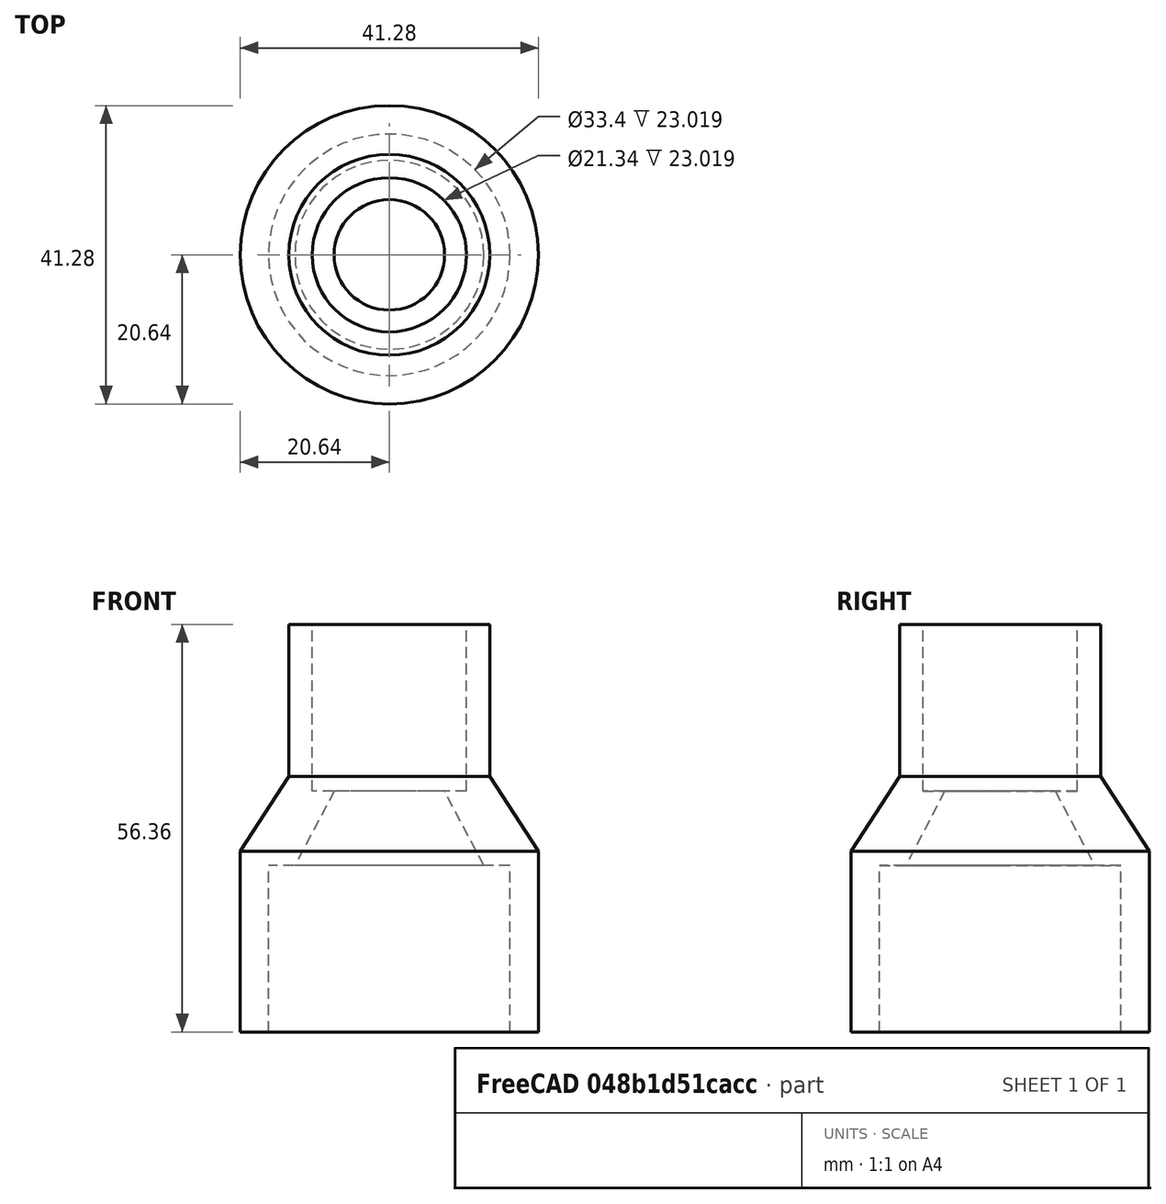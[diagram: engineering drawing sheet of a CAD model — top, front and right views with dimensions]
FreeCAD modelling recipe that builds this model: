
FCSTD DOCUMENT  (FreeCAD 0.17R13303 (Git))
Label: coupling-test
License: All rights reserved
LicenseURL: http://en.wikipedia.org/wiki/All_rights_reserved
objects: Part::Cylinder×4, Part::Cone×2, Part::MultiFuse×2, Part::Cut×1
note: 9 computed .brp shape members not serialized (recipe doc carries the construction recipe); baked Part::Feature solids carry a one-line shape summary decoded from their .brp

FEATURE [Part::Cylinder] Cylinder1
  Angle = 360
  AttacherType = Attacher::AttachEngine3D
  Height = 25.0057
  Radius = 20.6375
FEATURE [Part::Cone] Cone
  Angle = 360
  AttacherType = Attacher::AttachEngine3D
  Height = 10.3187
  Placement = pos=(0,0,25.0057) rot=(0,0,1;0rad)
  Radius1 = 20.6375
  Radius2 = 13.8906
FEATURE [Part::Cylinder] Cylinder2
  Angle = 360
  AttacherType = Attacher::AttachEngine3D
  Height = 21.0318
  Placement = pos=(0,0,35.3245) rot=(0,0,1;0rad)
  Radius = 13.8906
FEATURE [Part::MultiFuse] OuterParts
  Shapes = -> [Cylinder1,Cone,Cylinder2]
FEATURE [Part::Cylinder] Cylinder1i
  Angle = 360
  AttacherType = Attacher::AttachEngine3D
  Height = 23.0188
  Radius = 16.7005
FEATURE [Part::Cone] Cone001
  Angle = 360
  AttacherType = Attacher::AttachEngine3D
  Height = 10.3187
  Placement = pos=(0,0,23.0188) rot=(0,0,1;0rad)
  Radius1 = 13.0683
  Radius2 = 7.6454
FEATURE [Part::Cylinder] Cylinder2i
  Angle = 360
  AttacherType = Attacher::AttachEngine3D
  Height = 23.0188
  Placement = pos=(0,0,33.3375) rot=(0,0,1;0rad)
  Radius = 10.668
FEATURE [Part::MultiFuse] InnerParts
  Shapes = -> [Cylinder1i,Cone001,Cylinder2i]
FEATURE [Part::Cut] coupling  label="429-130"
  Base = -> OuterParts
  Tool = -> InnerParts
